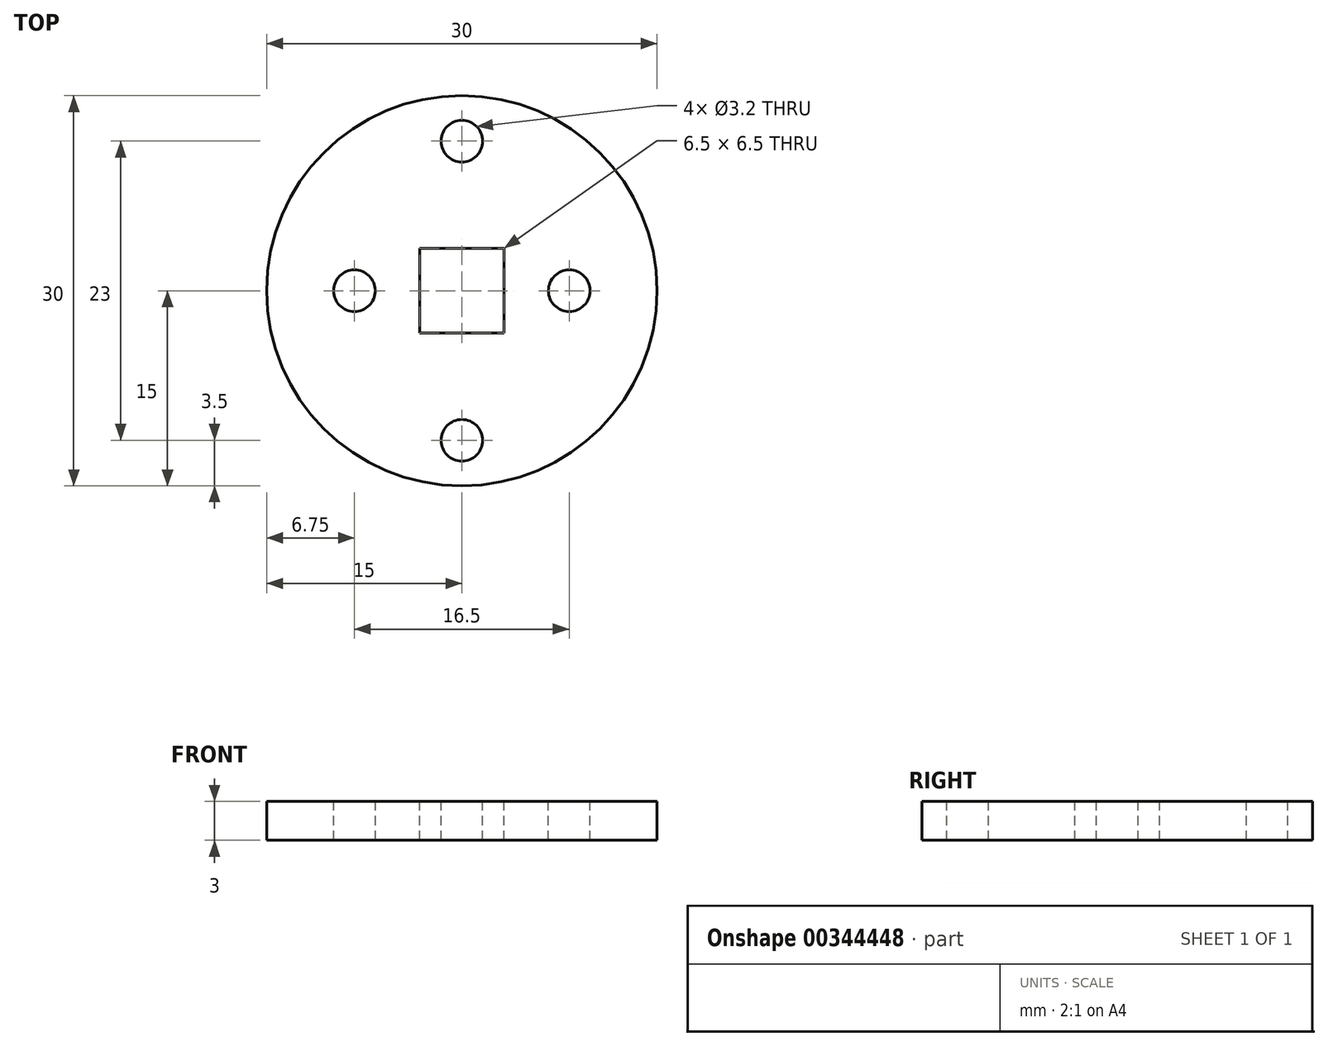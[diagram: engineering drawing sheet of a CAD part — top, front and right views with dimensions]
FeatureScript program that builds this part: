
annotation { "Feature Type Name" : "Feature", "Feature Type Description" : "" }
export const myFeature = defineFeature(function(context is Context, id is Id, definition is map)
    precondition{}
    {
        {
            var Q0;
            Q0=qCreatedBy(makeId("Top.planeOp"),FACE);
            var sketch = newSketch(context, id + "F0", { "sketchPlane" : qUnion([Q0])});
            skCircle(sketch, "E0", {"center": v(0, 0) * mm, "radius": 15 * mm});
            skSolve(sketch);
        }
        {
            var Q0;
            Q0=makeQuery(id+"F0.imprint","IMPRINT",FACE,{"disambiguationData":[TD([[makeQuery(id+"F0.imprint","IMPRINT",EDGE,{"derivedFrom":sQuery(id+"F0.wireOp",EDGE,"E0")}),1.0]])]});
            extrude(context, id + "F1", {"entities" : qUnion([Q0]), "depth" : 3 * mm});
        }
        {
            var Q0;
            Q0=makeQuery(id+"F1.opExtrude","CAP_FACE",FACE,{"disambiguationData":[OSD([sQuery(id+"F0.wireOp",EDGE,"E0")])],"isStart":false});
            var sketch = newSketch(context, id + "F2", { "sketchPlane" : qUnion([Q0])});
            skCircle(sketch, "E1", {"center": v(0, 11.5) * mm, "radius": 1.6 * mm});
            skCircle(sketch, "E2", {"center": v(0, -11.5) * mm, "radius": 1.6 * mm});
            skCircle(sketch, "E3", {"center": v(-8.25, 0) * mm, "radius": 1.6 * mm});
            skCircle(sketch, "E4", {"center": v(8.25, 0) * mm, "radius": 1.6 * mm});
            skLineSegment(sketch, "E5", {"start": v(-8.25, 0) * mm, "end": v(8.25, 0) * mm, "construction": true});
            skLineSegment(sketch, "E6", {"start": v(0, 11.5) * mm, "end": v(0, -11.5) * mm, "construction": true});
            skPoint(sketch, "E7", {"position": v(0, 0) * mm});
            skLineSegment(sketch, "E8.bottom", {"start": v(-3.25, 3.25) * mm, "end": v(3.25, 3.25) * mm});
            skLineSegment(sketch, "E8.top", {"start": v(-3.25, -3.25) * mm, "end": v(3.25, -3.25) * mm});
            skLineSegment(sketch, "E8.left", {"start": v(-3.25, 3.25) * mm, "end": v(-3.25, -3.25) * mm});
            skLineSegment(sketch, "E8.right", {"start": v(3.25, 3.25) * mm, "end": v(3.25, -3.25) * mm});
            skPoint(sketch, "E9", {"position": v(-3.25, 0) * mm});
            skPoint(sketch, "E10", {"position": v(0, 3.25) * mm});
            skSolve(sketch);
        }
        {
            var Q0;
            Q0 = qSketchRegion(id + "F2", true);
            extrude(context, id + "F3", {"entities" : qUnion([Q0]), "operationType" : NewBodyOperationType.REMOVE, "endBound" : BoundingType.UP_TO_NEXT, "oppositeDirection" : true, "depth" : 25 * mm});
        }
    });
